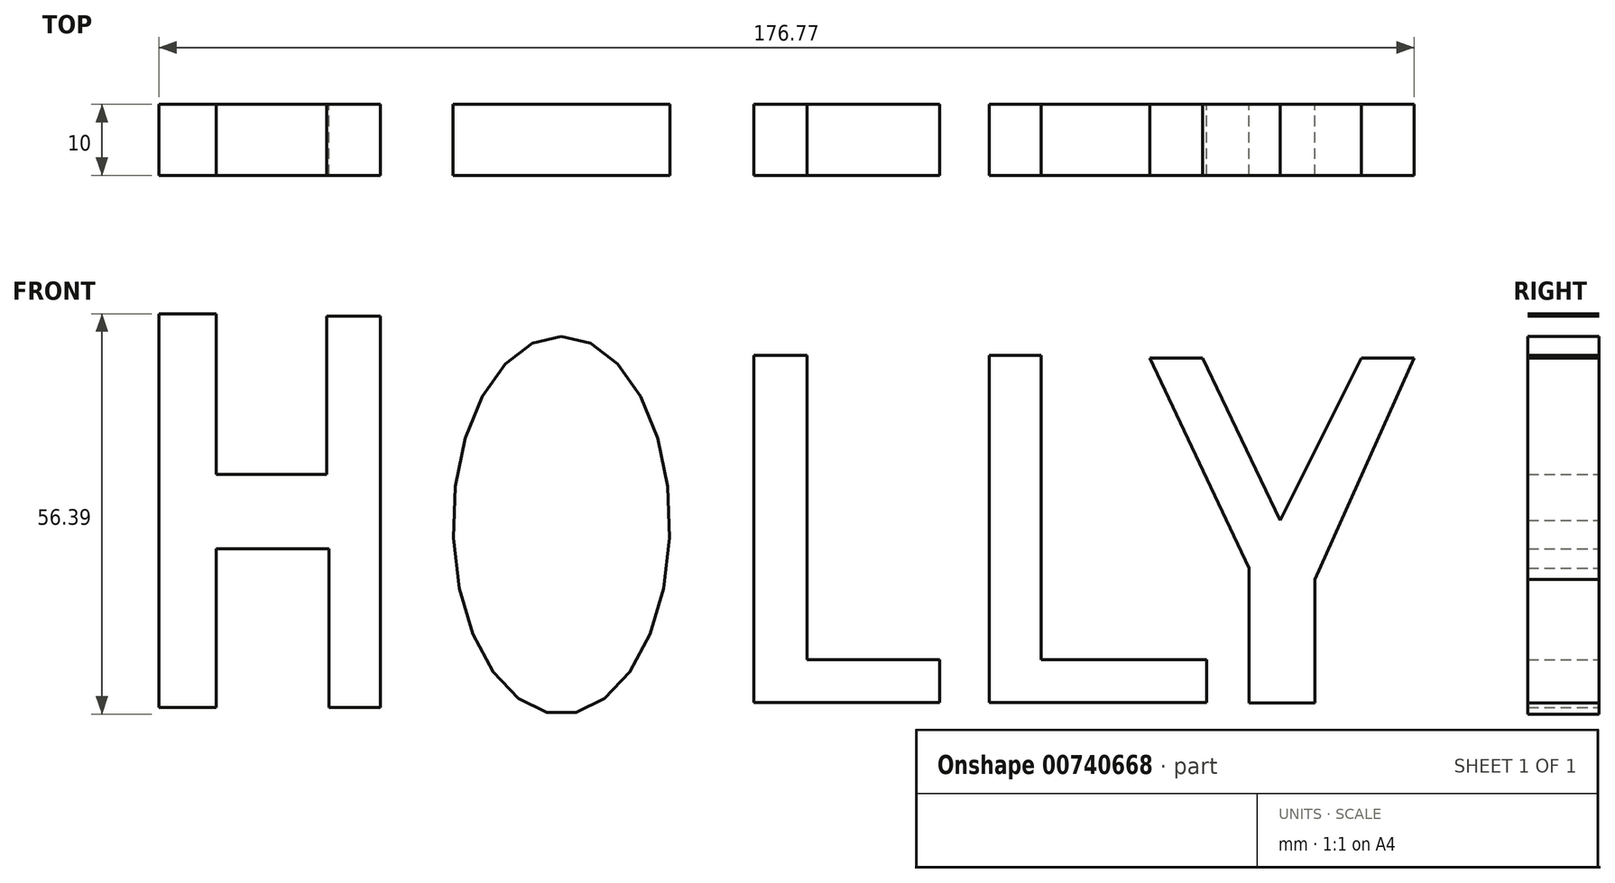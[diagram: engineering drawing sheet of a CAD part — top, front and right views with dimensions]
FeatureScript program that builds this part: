
annotation { "Feature Type Name" : "Feature", "Feature Type Description" : "" }
export const myFeature = defineFeature(function(context is Context, id is Id, definition is map)
    precondition{}
    {
        {
            var Q0;
            Q0=qCreatedBy(makeId("Front.planeOp"),FACE);
            var sketch = newSketch(context, id + "F0", { "sketchPlane" : qUnion([Q0])});
            skLineSegment(sketch, "E0", {"start": v(21.84, 50.86) * mm, "end": v(37.34, 50.86) * mm});
            skLineSegment(sketch, "E1", {"start": v(21.84, 40.38) * mm, "end": v(37.67, 40.38) * mm});
            skLineSegment(sketch, "E2", {"start": v(37.34, 73.15) * mm, "end": v(44.9, 73.15) * mm});
            skLineSegment(sketch, "E3", {"start": v(44.9, 73.15) * mm, "end": v(44.9, 18.02) * mm});
            skLineSegment(sketch, "E4", {"start": v(37.67, 18.02) * mm, "end": v(44.9, 18.02) * mm});
            skLineSegment(sketch, "E5", {"start": v(13.72, 73.48) * mm, "end": v(13.72, 18.02) * mm});
            skLineSegment(sketch, "E6", {"start": v(13.72, 18.02) * mm, "end": v(21.84, 18.02) * mm});
            skLineSegment(sketch, "E7", {"start": v(13.72, 73.48) * mm, "end": v(21.84, 73.48) * mm});
            skLineSegment(sketch, "E8", {"start": v(21.84, 73.48) * mm, "end": v(21.84, 50.86) * mm});
            skLineSegment(sketch, "E9", {"start": v(21.84, 18.02) * mm, "end": v(21.84, 40.38) * mm});
            skLineSegment(sketch, "E10", {"start": v(37.67, 40.38) * mm, "end": v(37.67, 18.02) * mm});
            skLineSegment(sketch, "E11", {"start": v(37.34, 50.86) * mm, "end": v(37.34, 73.15) * mm});
            skSolve(sketch);
        }
        {
            var Q0;
            Q0=qCreatedBy(makeId("Front.planeOp"),FACE);
            var sketch = newSketch(context, id + "F1", { "sketchPlane" : qUnion([Q0])});
            skLineSegment(sketch, "E12", {"start": v(97.5, 18.76) * mm, "end": v(97.5, 67.66) * mm});
            skLineSegment(sketch, "E13", {"start": v(97.5, 67.66) * mm, "end": v(105.02, 67.66) * mm});
            skLineSegment(sketch, "E14", {"start": v(105.02, 67.66) * mm, "end": v(105.02, 24.74) * mm});
            skLineSegment(sketch, "E15", {"start": v(105.02, 24.74) * mm, "end": v(123.64, 24.74) * mm});
            skLineSegment(sketch, "E16", {"start": v(97.5, 18.76) * mm, "end": v(123.64, 18.76) * mm});
            skLineSegment(sketch, "E17", {"start": v(123.64, 18.76) * mm, "end": v(123.64, 24.74) * mm});
            skEllipse(sketch, "E18", {"center": v(70.42, 43.7) * mm, "majorRadius": 26.61 * mm, "minorRadius": 15.27 * mm, "majorAxis": v(0, 1)});
            skLineSegment(sketch, "E19", {"start": v(130.63, 24.41) * mm, "end": v(130.63, 67.66) * mm});
            skLineSegment(sketch, "E20", {"start": v(137.95, 67.66) * mm, "end": v(137.95, 24.74) * mm});
            skLineSegment(sketch, "E21", {"start": v(137.95, 24.74) * mm, "end": v(161.23, 24.74) * mm});
            skLineSegment(sketch, "E22", {"start": v(130.63, 24.41) * mm, "end": v(130.63, 18.76) * mm});
            skLineSegment(sketch, "E23", {"start": v(130.63, 18.76) * mm, "end": v(162.57, 18.76) * mm});
            skLineSegment(sketch, "E24", {"start": v(161.23, 24.74) * mm, "end": v(161.23, 18.76) * mm});
            skLineSegment(sketch, "E25", {"start": v(161.23, 18.76) * mm, "end": v(162.57, 18.76) * mm});
            skLineSegment(sketch, "E26", {"start": v(137.95, 67.66) * mm, "end": v(130.63, 67.66) * mm});
            skLineSegment(sketch, "E27", {"start": v(153.23, 67.26) * mm, "end": v(160.68, 67.26) * mm});
            skLineSegment(sketch, "E28", {"start": v(160.68, 67.26) * mm, "end": v(171.57, 44.4) * mm});
            skLineSegment(sketch, "E29", {"start": v(167.2, 37.62) * mm, "end": v(167.2, 18.7) * mm});
            skLineSegment(sketch, "E30.MirrorCS", {"start": v(176.51, 36.05) * mm, "end": v(176.51, 18.7) * mm});
            skLineSegment(sketch, "E31.MirrorCS", {"start": v(183.03, 67.26) * mm, "end": v(171.57, 44.4) * mm});
            skLineSegment(sketch, "E32.MirrorCS", {"start": v(190.49, 67.26) * mm, "end": v(183.03, 67.26) * mm});
            skLineSegment(sketch, "E33", {"start": v(167.2, 18.7) * mm, "end": v(176.51, 18.7) * mm});
            skLineSegment(sketch, "E34", {"start": v(153.23, 67.26) * mm, "end": v(167.2, 37.62) * mm});
            skLineSegment(sketch, "E35", {"start": v(176.51, 36.05) * mm, "end": v(190.49, 67.26) * mm});
            skPoint(sketch, "E36.startSnap0", {"position": v(177.3, 55.83) * mm});
            skLineSegment(sketch, "E37", {"start": v(190.49, 67.26) * mm, "end": v(195.17, 67.26) * mm});
            skLineSegment(sketch, "E38", {"start": v(195.17, 67.26) * mm, "end": v(195.17, 18.76) * mm});
            skLineSegment(sketch, "E39", {"start": v(195.17, 18.76) * mm, "end": v(207.8, 38.71) * mm});
            skLineSegment(sketch, "E40", {"start": v(207.8, 38.71) * mm, "end": v(219.78, 18.76) * mm});
            skLineSegment(sketch, "E41", {"start": v(219.78, 18.76) * mm, "end": v(219.78, 67.26) * mm});
            skLineSegment(sketch, "E42", {"start": v(199.82, 67.26) * mm, "end": v(199.82, 38.71) * mm});
            skLineSegment(sketch, "E43", {"start": v(199.82, 38.71) * mm, "end": v(207.47, 48.7) * mm});
            skLineSegment(sketch, "E44", {"start": v(207.47, 48.7) * mm, "end": v(214.46, 38.71) * mm});
            skLineSegment(sketch, "E45", {"start": v(214.46, 38.71) * mm, "end": v(214.46, 67.26) * mm});
            skLineSegment(sketch, "E46", {"start": v(219.78, 67.26) * mm, "end": v(214.46, 67.26) * mm});
            skLineSegment(sketch, "E47", {"start": v(199.82, 67.26) * mm, "end": v(195.17, 67.26) * mm});
            skSolve(sketch);
        }
        {
            var Q0;
            Q0=makeQuery(id+"F1.imprint","IMPRINT",FACE,{"disambiguationData":[TD([[makeQuery(id+"F1.imprint","IMPRINT",EDGE,{"derivedFrom":sQuery(id+"F1.wireOp",EDGE,"E19")}),-1.0]])]});
            extrude(context, id + "F2", {"entities" : qUnion([Q0]), "depth" : 10 * mm, "offsetDistance" : 25 * mm});
        }
        {
            var Q0;
            Q0=makeQuery(id+"F0.imprint","IMPRINT",FACE,{"disambiguationData":[TD([[makeQuery(id+"F0.imprint","IMPRINT",EDGE,{"derivedFrom":sQuery(id+"F0.wireOp",EDGE,"E0")}),-1.0]])]});
            extrude(context, id + "F3", {"entities" : qUnion([Q0]), "depth" : 10 * mm, "offsetDistance" : 25 * mm});
        }
        {
            var Q0;
            Q0=makeQuery(id+"F1.imprint","IMPRINT",FACE,{"disambiguationData":[TD([[makeQuery(id+"F1.imprint","IMPRINT",EDGE,{"derivedFrom":sQuery(id+"F1.wireOp",EDGE,"E12")}),-1.0]])]});
            extrude(context, id + "F4", {"entities" : qUnion([Q0]), "depth" : 10 * mm, "offsetDistance" : 25 * mm});
        }
        {
            var Q0;
            Q0=makeQuery(id+"F1.imprint","IMPRINT",FACE,{"disambiguationData":[TD([[makeQuery(id+"F1.imprint","IMPRINT",EDGE,{"derivedFrom":sQuery(id+"F1.wireOp",EDGE,"E18")}),1.0]])]});
            extrude(context, id + "F5", {"entities" : qUnion([Q0]), "depth" : 10 * mm, "offsetDistance" : 25 * mm});
        }
        {
            var Q0;
            Q0=makeQuery(id+"F1.imprint","IMPRINT",FACE,{"disambiguationData":[TD([[makeQuery(id+"F1.imprint","IMPRINT",EDGE,{"derivedFrom":sQuery(id+"F1.wireOp",EDGE,"E27")}),-1.0]])]});
            extrude(context, id + "F6", {"entities" : qUnion([Q0]), "depth" : 10 * mm, "offsetDistance" : 25 * mm});
        }
    });
